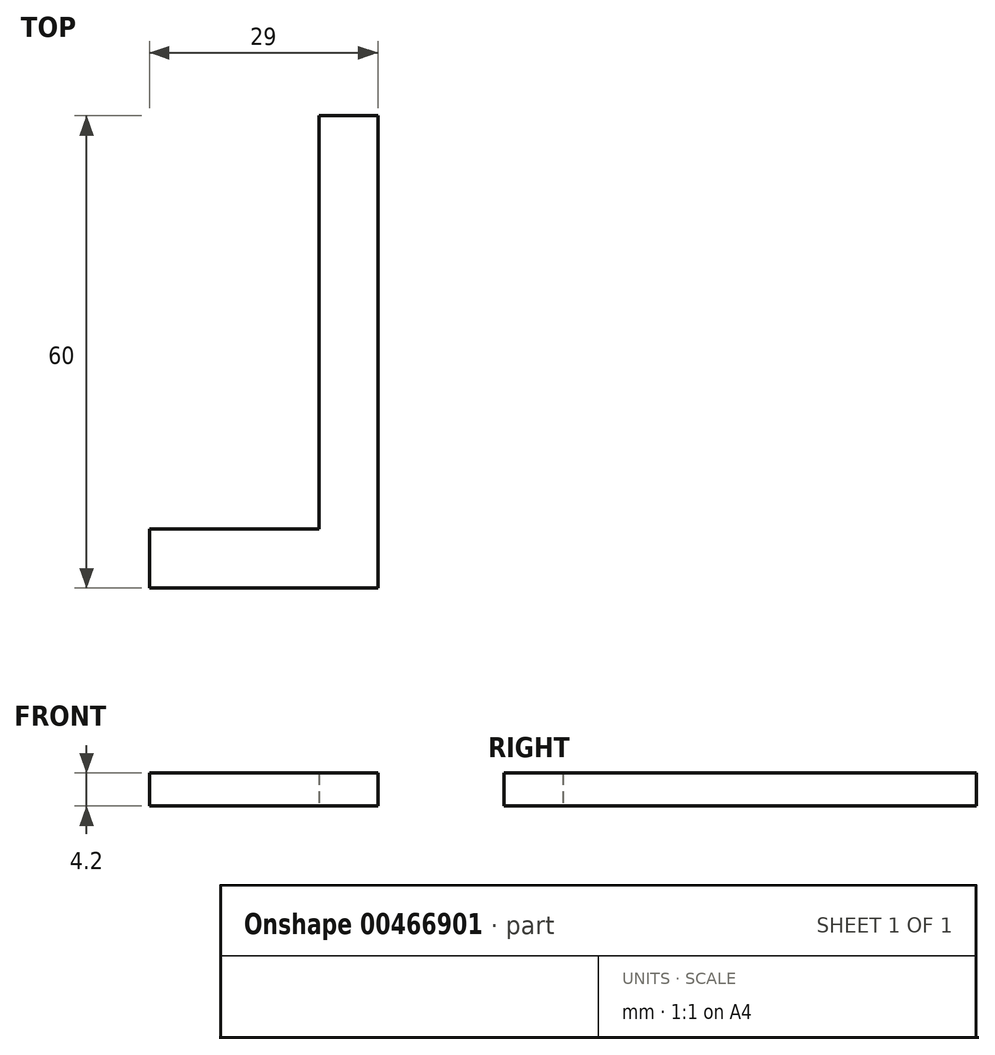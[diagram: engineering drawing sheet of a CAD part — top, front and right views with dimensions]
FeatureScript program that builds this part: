
annotation { "Feature Type Name" : "Feature", "Feature Type Description" : "" }
export const myFeature = defineFeature(function(context is Context, id is Id, definition is map)
    precondition{}
    {
        {
            var Q0;
            Q0=qCreatedBy(makeId("Top.planeOp"),FACE);
            var sketch = newSketch(context, id + "F0", { "sketchPlane" : qUnion([Q0])});
            skLineSegment(sketch, "E0.bottom", {"start": v(-14.5, -3.75) * mm, "end": v(14.5, -3.75) * mm});
            skLineSegment(sketch, "E0.top", {"start": v(-14.5, 3.75) * mm, "end": v(14.5, 3.75) * mm});
            skLineSegment(sketch, "E0.left", {"start": v(-14.5, -3.75) * mm, "end": v(-14.5, 3.75) * mm});
            skLineSegment(sketch, "E0.right", {"start": v(14.5, -3.75) * mm, "end": v(14.5, 3.75) * mm});
            skPoint(sketch, "E0.middle", {"position": v(0, 0) * mm});
            skLineSegment(sketch, "E1.bottom", {"start": v(14.5, -3.75) * mm, "end": v(7, -3.75) * mm});
            skLineSegment(sketch, "E1.top", {"start": v(14.5, 56.25) * mm, "end": v(7, 56.25) * mm});
            skLineSegment(sketch, "E1.left", {"start": v(14.5, -3.75) * mm, "end": v(14.5, 56.25) * mm});
            skLineSegment(sketch, "E1.right", {"start": v(7, -3.75) * mm, "end": v(7, 56.25) * mm});
            skSolve(sketch);
        }
        {
            var Q0;
            Q0 = qSketchRegion(id + "F0", true);
            extrude(context, id + "F1", {"entities" : qUnion([Q0]), "depth" : 4.2 * mm});
        }
    });
